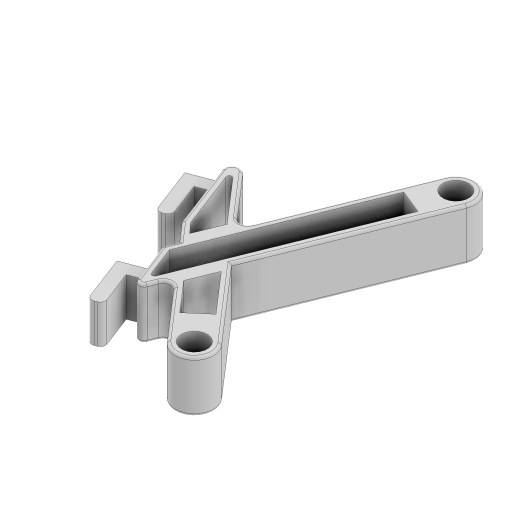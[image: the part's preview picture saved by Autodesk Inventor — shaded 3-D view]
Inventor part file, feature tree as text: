
AUTODESK INVENTOR PART (.ipt)
format: ipt  version: 2024 (Build 280153000, 153)  size: 346,624 bytes
history: native  units: mm
features: extrude x9, sketch x7, fillet x7
ambient origin geometry x8: Origin, YZ Plane, XZ Plane, XY Plane, X Axis, Y Axis, Z Axis, Center Point
bodies: Solid1 (feature_tree)
feature tree (23):
  sketch  "Sketch1"  dims[d0=10.0mm d1=10.0mm d2=101.8mm]
  extrude  "Extrusion1"  Depth=10.0mm
  fillet  "Fillet1"  Radius=101.8mm
  extrude  "Extrusion9"  Depth=15.0mm
  extrude  "Extrusion10"  Depth=11.885692mm
  sketch  "Sketch16"  dims[d20=8.569567mm d21=11.885692mm d23=11.885692mm d24=22.017724mm]
  extrude  "Extrusion11"  Depth=11.885692mm
  fillet  "Fillet10"  Radius=11.885692mm
  fillet  "Fillet12"  Radius=22.017724mm
  extrude  "Extrusion13"  Depth=20.0mm TaperAngle=0.0deg
  extrude  "Extrusion14"  Depth=15.0mm
  fillet  "Fillet17"  Radius=5.0mm
  fillet  "Fillet18"  Radius=15.0mm
  fillet  "Fillet19"  Radius=5.0mm
  extrude  "Extrusion15"  Depth=15.0mm
  sketch  "Sketch19"  dims[d42=3.0mm d74=15.0mm d75=5.0mm d76=15.0mm d77=5.0mm]
  extrude  "Extrusion16"  Depth=5.0mm
  extrude  "Extrusion17"  Depth=15.0mm
  fillet  "Fillet20"  Radius=5.0mm
  sketch  "Sketch12"  dims[d3=15.0mm d14=77.9mm]
  sketch  "Sketch13"  dims[d15=8.569567mm d17=11.885692mm]
  sketch  "Sketch18"  dims[d25=44.159832mm d26=20.0mm d27=0.0mm]
  sketch  "Sketch20"  dims[d78=0.0mm d79=0.0mm d80=15.0mm d81=5.0mm d82=15.0mm d83=5.0mm d84=0.0mm d85=0.0mm d87=5.0mm d88=2.5mm d89=2.5mm d90=2.5mm d91=0.0mm d92=0.0mm d95=2.5mm d96=2.5mm d97=5.0mm d98=5.0mm d99=5.0mm d104=1.0mm d106=2.0mm d115=20.0mm d116=0.0mm d118=20.0mm d119=0.0mm d120=1.0mm d121=3.0mm d122=1.0mm d123=5.0mm d124=15.0mm d125=5.0mm d126=46.0mm d127=10.0mm d128=0.0mm d129=3.51mm d130=5.0mm d131=15.0mm d132=5.0mm d133=15.0mm d134=15.0mm d135=0.0mm d136=15.0mm d137=0.0mm d138=2.0mm d72=0.0mm d73=0.0mm]
